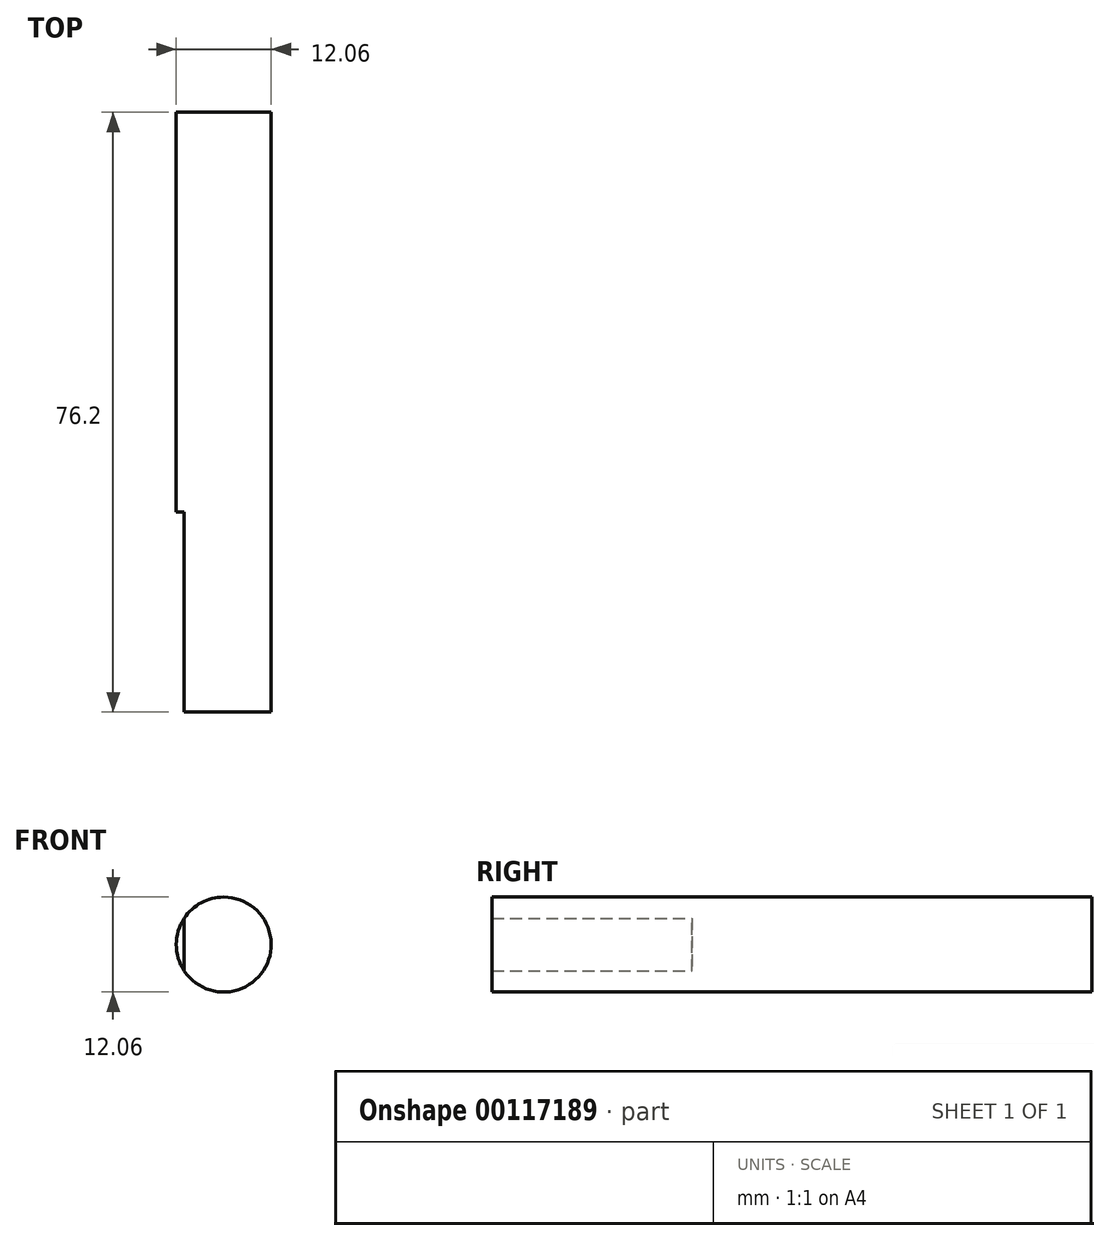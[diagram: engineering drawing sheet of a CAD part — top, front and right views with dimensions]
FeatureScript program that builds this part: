
annotation { "Feature Type Name" : "Feature", "Feature Type Description" : "" }
export const myFeature = defineFeature(function(context is Context, id is Id, definition is map)
    precondition{}
    {
        {
            var Q0;
            Q0=qCreatedBy(makeId("Front.planeOp"),FACE);
            var sketch = newSketch(context, id + "F0", { "sketchPlane" : qUnion([Q0])});
            skArc(sketch, "E0", {"start": v(-5.02, -3.35) * mm, "mid": v(6.03, 0) * mm, "end": v(-5.02, 3.35) * mm});
            skLineSegment(sketch, "E1", {"start": v(6.03, 0) * mm, "end": v(-5.02, 0) * mm, "construction": true});
            skLineSegment(sketch, "E2", {"start": v(-5.02, 3.35) * mm, "end": v(-5.02, -3.35) * mm});
            skSolve(sketch);
        }
        {
            var Q0;
            Q0 = qSketchRegion(id + "F0", true);
            extrude(context, id + "F1", {"entities" : qUnion([Q0]), "depth" : 25.4 * mm});
        }
        {
            var Q0;
            Q0=makeQuery(id+"F1.opExtrude","CAP_FACE",FACE,{"disambiguationData":[OSD([sQuery(id+"F0.wireOp",EDGE,"E0"),sQuery(id+"F0.wireOp",EDGE,"E2")])],"isStart":true});
            var sketch = newSketch(context, id + "F2", { "sketchPlane" : qUnion([Q0])});
            skCircle(sketch, "E3", {"center": v(0, 0) * mm, "radius": 6.03 * mm});
            skSolve(sketch);
        }
        {
            var Q0;
            Q0 = qSketchRegion(id + "F2", true);
            extrude(context, id + "F3", {"entities" : qUnion([Q0]), "operationType" : NewBodyOperationType.ADD, "depth" : 50.8 * mm});
        }
    });
